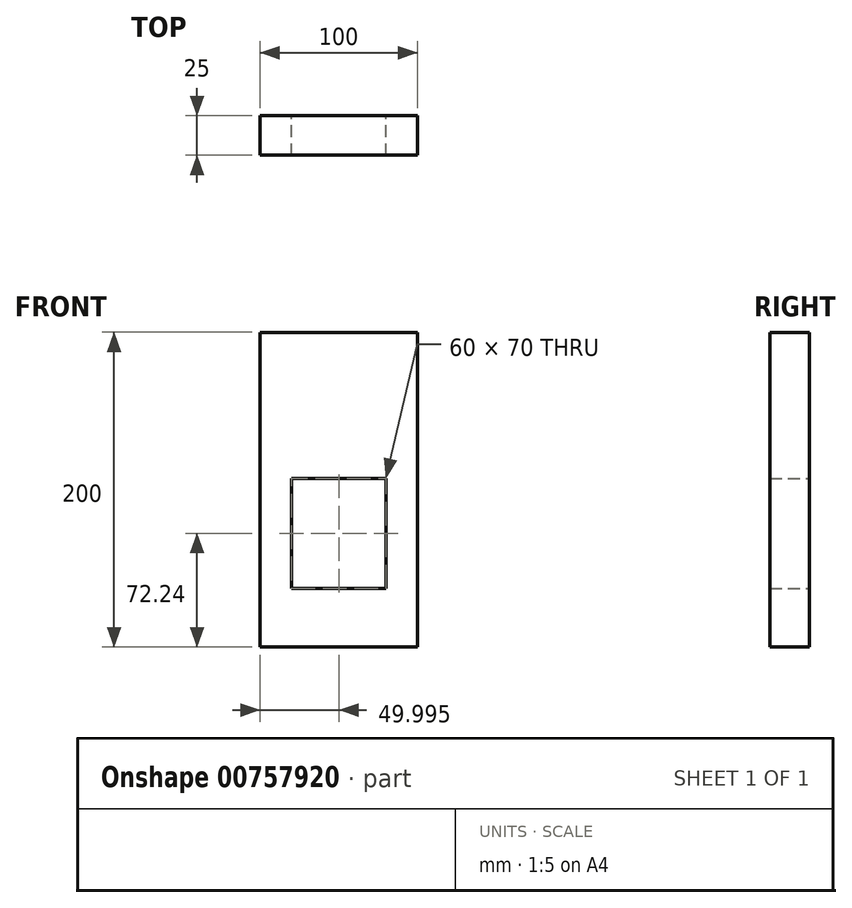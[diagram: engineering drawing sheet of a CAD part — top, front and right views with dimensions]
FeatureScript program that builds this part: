
annotation { "Feature Type Name" : "Feature", "Feature Type Description" : "" }
export const myFeature = defineFeature(function(context is Context, id is Id, definition is map)
    precondition{}
    {
        {
            var Q0;
            Q0=qCreatedBy(makeId("Front.planeOp"),FACE);
            var sketch = newSketch(context, id + "F0", { "sketchPlane" : qUnion([Q0])});
            skLineSegment(sketch, "E0.bottom", {"start": v(-50.42, 162.76) * mm, "end": v(49.58, 162.76) * mm});
            skLineSegment(sketch, "E0.top", {"start": v(-50.42, -37.24) * mm, "end": v(49.58, -37.24) * mm});
            skLineSegment(sketch, "E0.left", {"start": v(-50.42, 162.76) * mm, "end": v(-50.42, -37.24) * mm});
            skLineSegment(sketch, "E0.right", {"start": v(49.58, 162.76) * mm, "end": v(49.58, -37.24) * mm});
            skLineSegment(sketch, "E1.bottom", {"start": v(-30.42, 70) * mm, "end": v(29.58, 70) * mm});
            skLineSegment(sketch, "E1.top", {"start": v(-30.42, 0) * mm, "end": v(29.58, 0) * mm});
            skLineSegment(sketch, "E1.left", {"start": v(-30.42, 70) * mm, "end": v(-30.42, 0) * mm});
            skLineSegment(sketch, "E1.right", {"start": v(29.58, 70) * mm, "end": v(29.58, 0) * mm});
            skSolve(sketch);
        }
        {
            var Q0;
            Q0 = qSketchRegion(id + "F0", true);
            extrude(context, id + "F1", {"entities" : qUnion([Q0]), "depth" : 25 * mm, "offsetDistance" : 25 * mm});
        }
    });
